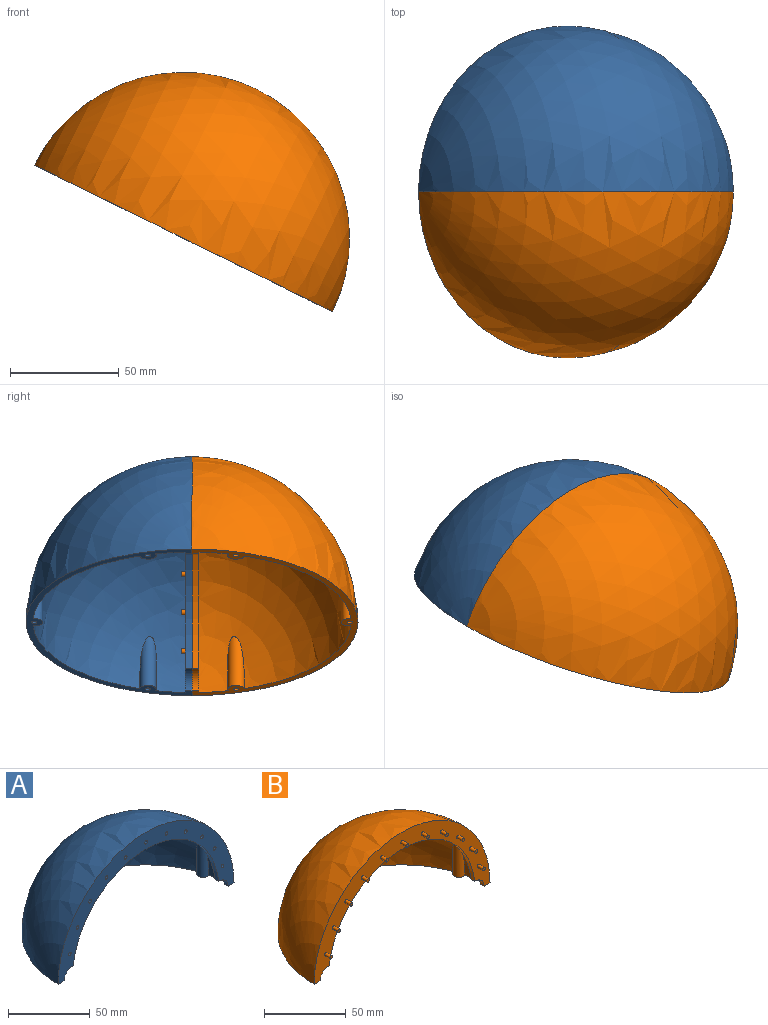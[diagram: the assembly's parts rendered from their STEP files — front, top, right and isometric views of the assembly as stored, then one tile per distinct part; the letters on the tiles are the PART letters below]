
ASSEMBLY  parts=2 mates=1
PART A: 28 faces, bbox 152.4x76.2x76.2 mm
  f0: sphere r=73.03mm, area 15494mm2, adj f3,f4,f6,f7,f8
  f1: sphere r=76.2mm, area 18241.5mm2, adj f2,f3
  f2: plane 152.4x76.2mm, normal (0,-1,0), area 2640.9mm2, adj f1,f3,f5,f15,f16,f17,f18,f19
  f3: plane 152.4x76.2mm, normal (0,0,-1), area 824mm2, adj f0,f1,f2,f4,f6,f7,f8,f9
  f4: plane 145.91x72.96mm, normal (0,1,0), area 1880.9mm2, adj f0,f3,f5,f15,f16,f17,f18,f19
  f5: cylinder r=63.5mm len=126.09mm, axis (0,-1,0), area 585mm2, adj f2,f4,f15,f16
  f6: cylinder r=3.81mm len=25.09mm, axis (0,0,-1), area 248mm2, adj f0,f3
  f7: cylinder r=3.81mm len=25.09mm, axis (0,0,-1), area 248mm2, adj f0,f3
  f8: cylinder r=3.81mm len=25.09mm, axis (0,0,-1), area 248mm2, adj f0,f3
  f9: cylinder r=1.23mm len=10.16mm, axis (0,0,-1), area 78.6mm2, adj f3,f10
  f10: plane 2.46x2.46mm, normal (0,0,-1), area 4.8mm2, adj f9
  f11: cylinder r=1.23mm len=10.16mm, axis (0,0,-1), area 78.6mm2, adj f3,f12
  f12: plane 2.46x2.46mm, normal (0,0,-1), area 4.8mm2, adj f11
  f13: cylinder r=1.23mm len=10.16mm, axis (0,0,-1), area 78.6mm2, adj f3,f14
  f14: plane 2.46x2.46mm, normal (0,0,-1), area 4.8mm2, adj f13
  f15: cylinder r=7.62mm len=8.08mm, axis (0,-1,0), area 39.5mm2, adj f2,f3,f4,f5
  f16: cylinder r=7.62mm len=8.08mm, axis (0,-1,0), area 39.5mm2, adj f2,f3,f4,f5
  f17: cylinder r=1.23mm len=3.18mm, axis (0,-1,0), area 24.6mm2, adj f2,f4
  f18: cylinder r=1.23mm len=3.18mm, axis (0,-1,0), area 24.6mm2, adj f2,f4
  f19: cylinder r=1.23mm len=3.18mm, axis (0,-1,0), area 24.6mm2, adj f2,f4
  f20: cylinder r=1.23mm len=3.18mm, axis (0,-1,0), area 24.6mm2, adj f2,f4
  f21: cylinder r=1.23mm len=3.18mm, axis (0,-1,0), area 24.6mm2, adj f2,f4
  f22: cylinder r=1.23mm len=3.18mm, axis (0,-1,0), area 24.6mm2, adj f2,f4
  f23: cylinder r=1.23mm len=3.18mm, axis (0,-1,0), area 24.6mm2, adj f2,f4
  f24: cylinder r=1.23mm len=3.18mm, axis (0,-1,0), area 24.6mm2, adj f2,f4
  f25: cylinder r=1.23mm len=3.18mm, axis (0,-1,0), area 24.6mm2, adj f2,f4
  f26: cylinder r=1.23mm len=3.18mm, axis (0,-1,0), area 24.6mm2, adj f2,f4
  f27: cylinder r=1.23mm len=3.18mm, axis (0,-1,0), area 24.6mm2, adj f2,f4
PART B: 39 faces, bbox 152.4x81x76.2 mm
  f0: sphere r=73.03mm, area 15494mm2, adj f3,f4,f6,f7,f8
  f1: sphere r=76.2mm, area 18241.5mm2, adj f2,f3
  f2: plane 152.4x76.2mm, normal (0,-1,0), area 2648.2mm2, adj f1,f3,f5,f15,f16,f17,f19,f21
  f3: plane 152.4x76.2mm, normal (0,0,-1), area 824mm2, adj f0,f1,f2,f4,f6,f7,f8,f9
  f4: plane 145.91x72.96mm, normal (0,1,0), area 1933.3mm2, adj f0,f3,f5,f15,f16
  f5: cylinder r=63.5mm len=126.09mm, axis (0,-1,0), area 585mm2, adj f2,f4,f15,f16
  f6: cylinder r=3.81mm len=25.09mm, axis (0,0,-1), area 248mm2, adj f0,f3
  f7: cylinder r=3.81mm len=25.09mm, axis (0,0,-1), area 248mm2, adj f0,f3
  f8: cylinder r=3.81mm len=25.09mm, axis (0,0,-1), area 248mm2, adj f0,f3
  f9: cylinder r=1.23mm len=10.16mm, axis (0,0,-1), area 78.6mm2, adj f3,f10
  f10: plane 2.46x2.46mm, normal (0,0,-1), area 4.8mm2, adj f9
  f11: cylinder r=1.23mm len=10.16mm, axis (0,0,-1), area 78.6mm2, adj f3,f12
  f12: plane 2.46x2.46mm, normal (0,0,-1), area 4.8mm2, adj f11
  f13: cylinder r=1.23mm len=10.16mm, axis (0,0,-1), area 78.6mm2, adj f3,f14
  f14: plane 2.46x2.46mm, normal (0,0,-1), area 4.8mm2, adj f13
  f15: cylinder r=7.62mm len=8.08mm, axis (0,-1,0), area 39.5mm2, adj f2,f3,f4,f5
  f16: cylinder r=7.62mm len=8.08mm, axis (0,-1,0), area 39.5mm2, adj f2,f3,f4,f5
  f17: cylinder r=1.14mm len=4.76mm, axis (0,1,0), area 34.2mm2, adj f2,f18
  f18: plane 2.29x2.29mm, normal (0,-1,0), area 4.1mm2, adj f17
  f19: cylinder r=1.14mm len=4.76mm, axis (0,1,0), area 34.2mm2, adj f2,f20
  f20: plane 2.29x2.29mm, normal (0,-1,0), area 4.1mm2, adj f19
  f21: cylinder r=1.14mm len=4.76mm, axis (0,1,0), area 34.2mm2, adj f2,f22
  f22: plane 2.29x2.29mm, normal (0,-1,0), area 4.1mm2, adj f21
  f23: cylinder r=1.14mm len=4.76mm, axis (0,1,0), area 34.2mm2, adj f2,f24
  f24: plane 2.29x2.29mm, normal (0,-1,0), area 4.1mm2, adj f23
  f25: cylinder r=1.14mm len=4.76mm, axis (0,1,0), area 34.2mm2, adj f2,f26
  f26: plane 2.29x2.29mm, normal (0,-1,0), area 4.1mm2, adj f25
  f27: cylinder r=1.14mm len=4.76mm, axis (0,1,0), area 34.2mm2, adj f2,f28
  f28: plane 2.29x2.29mm, normal (0,-1,0), area 4.1mm2, adj f27
  f29: cylinder r=1.14mm len=4.76mm, axis (0,1,0), area 34.2mm2, adj f2,f30
  f30: plane 2.29x2.29mm, normal (0,-1,0), area 4.1mm2, adj f29
  f31: cylinder r=1.14mm len=4.76mm, axis (0,1,0), area 34.2mm2, adj f2,f32
  f32: plane 2.29x2.29mm, normal (0,-1,0), area 4.1mm2, adj f31
  f33: cylinder r=1.14mm len=4.76mm, axis (0,1,0), area 34.2mm2, adj f2,f34
  f34: plane 2.29x2.29mm, normal (0,-1,0), area 4.1mm2, adj f33
  f35: cylinder r=1.14mm len=4.76mm, axis (0,1,0), area 34.2mm2, adj f2,f36
  f36: plane 2.29x2.29mm, normal (0,-1,0), area 4.1mm2, adj f35
  f37: cylinder r=1.14mm len=4.76mm, axis (0,1,0), area 34.2mm2, adj f2,f38
  f38: plane 2.29x2.29mm, normal (0,-1,0), area 4.1mm2, adj f37
PLACE A rot(axis=(0,1,0),26.2deg) t=(-114.18,30.38,22.1)mm
PLACE B rot(axis=(-0.23,0,-0.97),180deg) t=(-114.18,30.38,22.1)mm
MATE fastened B.f27 <-> A.f25  axis (0,1,0) through (-46.9,30.38,8.79)mm
